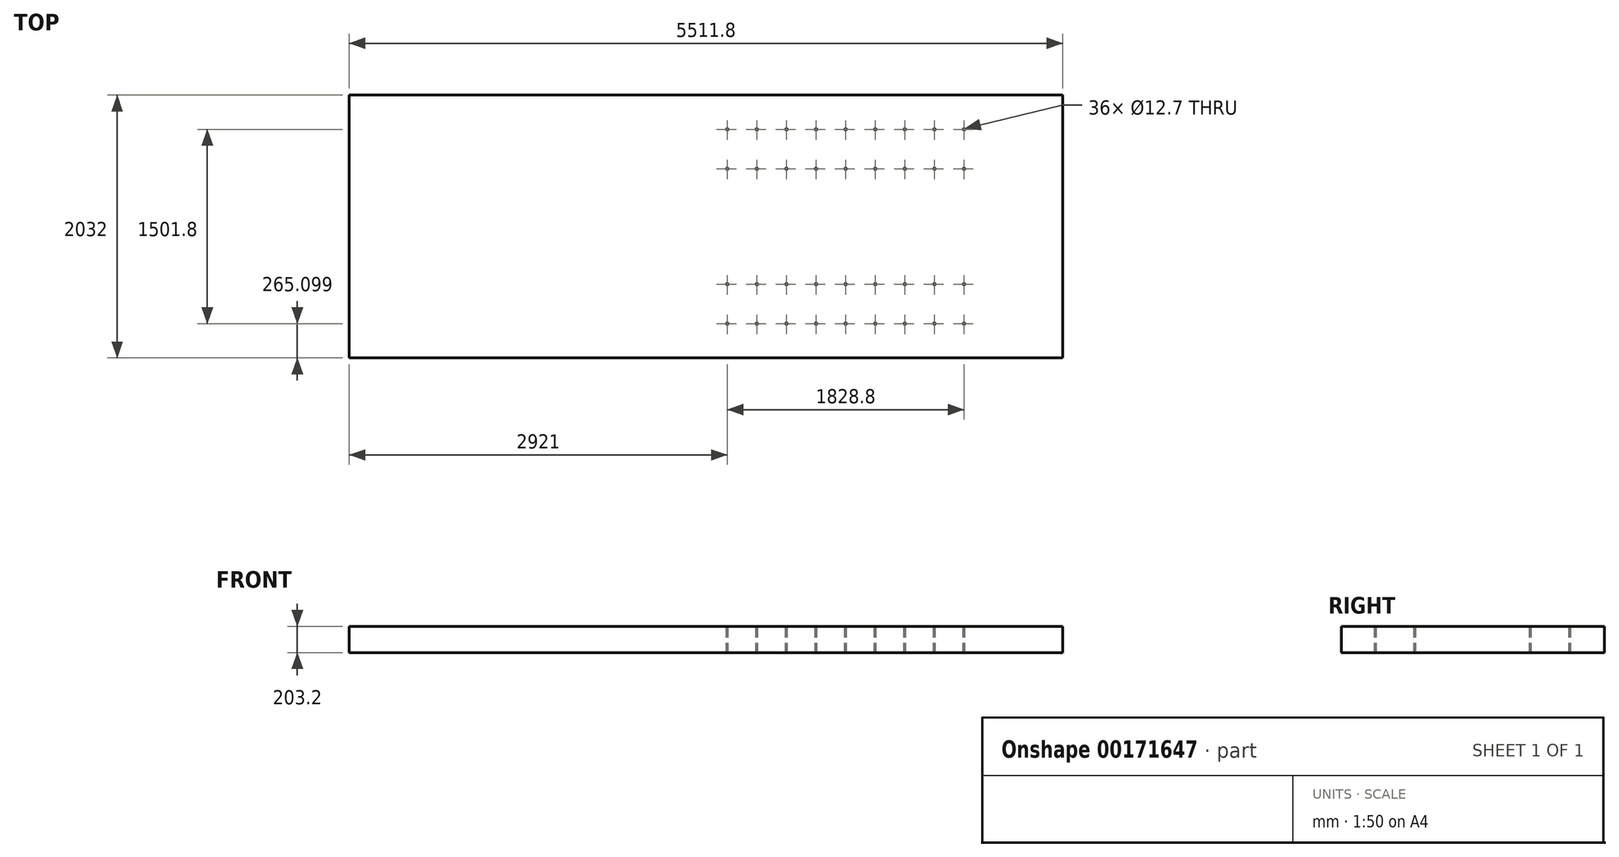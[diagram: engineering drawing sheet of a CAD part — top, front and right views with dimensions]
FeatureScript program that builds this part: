
annotation { "Feature Type Name" : "Feature", "Feature Type Description" : "" }
export const myFeature = defineFeature(function(context is Context, id is Id, definition is map)
    precondition{}
    {
        {
            var Q0;
            Q0=qCreatedBy(makeId("Top.planeOp"),FACE);
            var sketch = newSketch(context, id + "F0", { "sketchPlane" : qUnion([Q0])});
            skLineSegment(sketch, "E0.bottom", {"start": v(2755.9, 1016) * mm, "end": v(-2755.9, 1016) * mm});
            skLineSegment(sketch, "E0.top", {"start": v(2755.9, -1016) * mm, "end": v(-2755.9, -1016) * mm});
            skLineSegment(sketch, "E0.left", {"start": v(2755.9, 1016) * mm, "end": v(2755.9, -1016) * mm});
            skLineSegment(sketch, "E0.right", {"start": v(-2755.9, 1016) * mm, "end": v(-2755.9, -1016) * mm});
            skSolve(sketch);
        }
        {
            var Q0;
            Q0=makeQuery(id+"F0.imprint","IMPRINT",FACE,{"disambiguationData":[TD([[makeQuery(id+"F0.imprint","IMPRINT",EDGE,{"derivedFrom":sQuery(id+"F0.wireOp",EDGE,"E0.bottom")}),1.0]])]});
            extrude(context, id + "F1", {"entities" : qUnion([Q0]), "depth" : 203.2 * mm});
        }
        {
            var Q0;
            Q0=makeQuery(id+"F1.opExtrude","CAP_FACE",FACE,{"disambiguationData":[OSD([sQuery(id+"F0.wireOp",EDGE,"E0.bottom"),sQuery(id+"F0.wireOp",EDGE,"E0.top"),sQuery(id+"F0.wireOp",EDGE,"E0.left"),sQuery(id+"F0.wireOp",EDGE,"E0.right")])],"isStart":true});
            var sketch = newSketch(context, id + "F2", { "sketchPlane" : qUnion([Q0])});
            skPoint(sketch, "E1", {"position": v(1993.9, 750.9) * mm});
            skPoint(sketch, "E2", {"position": v(1765.3, 750.9) * mm});
            skPoint(sketch, "E3", {"position": v(1536.7, 750.9) * mm});
            skPoint(sketch, "E4", {"position": v(1079.5, 750.9) * mm});
            skPoint(sketch, "E5", {"position": v(393.7, 750.9) * mm});
            skPoint(sketch, "E6", {"position": v(622.3, 750.9) * mm});
            skPoint(sketch, "E7", {"position": v(850.9, 750.9) * mm});
            skPoint(sketch, "E8", {"position": v(1308.1, 750.9) * mm});
            skPoint(sketch, "E9", {"position": v(165.1, 750.9) * mm});
            skPoint(sketch, "E10.MirrorP", {"position": v(1993.9, 446.1) * mm});
            skPoint(sketch, "E11.MirrorP", {"position": v(1765.3, 446.1) * mm});
            skPoint(sketch, "E12.MirrorP", {"position": v(1536.7, 446.1) * mm});
            skPoint(sketch, "E13.MirrorP", {"position": v(1308.1, 446.1) * mm});
            skPoint(sketch, "E14.MirrorP", {"position": v(1079.5, 446.1) * mm});
            skPoint(sketch, "E15.MirrorP", {"position": v(850.9, 446.1) * mm});
            skPoint(sketch, "E16.MirrorP", {"position": v(622.3, 446.1) * mm});
            skPoint(sketch, "E17.MirrorP", {"position": v(393.7, 446.1) * mm});
            skPoint(sketch, "E18.MirrorP", {"position": v(165.1, 446.1) * mm});
            skPoint(sketch, "E19.MirrorP", {"position": v(1993.9, -446.1) * mm});
            skPoint(sketch, "E20.MirrorP", {"position": v(1308.1, -750.9) * mm});
            skPoint(sketch, "E21.MirrorP", {"position": v(1765.3, -446.1) * mm});
            skPoint(sketch, "E22.MirrorP", {"position": v(850.9, -446.1) * mm});
            skPoint(sketch, "E23.MirrorP", {"position": v(622.3, -446.1) * mm});
            skPoint(sketch, "E24.MirrorP", {"position": v(1079.5, -446.1) * mm});
            skPoint(sketch, "E25.MirrorP", {"position": v(1079.5, -750.9) * mm});
            skPoint(sketch, "E26.MirrorP", {"position": v(850.9, -750.9) * mm});
            skPoint(sketch, "E27.MirrorP", {"position": v(393.7, -750.9) * mm});
            skPoint(sketch, "E28.MirrorP", {"position": v(1993.9, -750.9) * mm});
            skPoint(sketch, "E29.MirrorP", {"position": v(165.1, -446.1) * mm});
            skPoint(sketch, "E30.MirrorP", {"position": v(1308.1, -446.1) * mm});
            skPoint(sketch, "E31.MirrorP", {"position": v(165.1, -750.9) * mm});
            skPoint(sketch, "E32.MirrorP", {"position": v(1765.3, -750.9) * mm});
            skPoint(sketch, "E33.MirrorP", {"position": v(1536.7, -750.9) * mm});
            skPoint(sketch, "E34.MirrorP", {"position": v(1536.7, -446.1) * mm});
            skPoint(sketch, "E35.MirrorP", {"position": v(622.3, -750.9) * mm});
            skPoint(sketch, "E36.MirrorP", {"position": v(393.7, -446.1) * mm});
            skSolve(sketch);
        }
        {
            var Q0;
            Q0=sQuery(id+"F2.wireOp",VERTEX,"E5");
            var Q1;
            Q1=sQuery(id+"F2.wireOp",VERTEX,"E4");
            var Q2;
            Q2=sQuery(id+"F2.wireOp",VERTEX,"E3");
            var Q3;
            Q3=sQuery(id+"F2.wireOp",VERTEX,"E2");
            var Q4;
            Q4=sQuery(id+"F2.wireOp",VERTEX,"E1");
            var Q5;
            Q5=sQuery(id+"F2.wireOp",VERTEX,"E32.MirrorP");
            var Q6;
            Q6=sQuery(id+"F2.wireOp",VERTEX,"E15.MirrorP");
            var Q7;
            Q7=sQuery(id+"F2.wireOp",VERTEX,"E33.MirrorP");
            var Q8;
            Q8=sQuery(id+"F2.wireOp",VERTEX,"E14.MirrorP");
            var Q9;
            Q9=sQuery(id+"F2.wireOp",VERTEX,"E13.MirrorP");
            var Q10;
            Q10=sQuery(id+"F2.wireOp",VERTEX,"E35.MirrorP");
            var Q11;
            Q11=sQuery(id+"F2.wireOp",VERTEX,"E12.MirrorP");
            var Q12;
            Q12=sQuery(id+"F2.wireOp",VERTEX,"E36.MirrorP");
            var Q13;
            Q13=sQuery(id+"F2.wireOp",VERTEX,"E19.MirrorP");
            var Q14;
            Q14=sQuery(id+"F2.wireOp",VERTEX,"E30.MirrorP");
            var Q15;
            Q15=sQuery(id+"F2.wireOp",VERTEX,"E25.MirrorP");
            var Q16;
            Q16=sQuery(id+"F2.wireOp",VERTEX,"E27.MirrorP");
            var Q17;
            Q17=sQuery(id+"F2.wireOp",VERTEX,"E11.MirrorP");
            var Q18;
            Q18=sQuery(id+"F2.wireOp",VERTEX,"E16.MirrorP");
            var Q19;
            Q19=sQuery(id+"F2.wireOp",VERTEX,"E34.MirrorP");
            var Q20;
            Q20=sQuery(id+"F2.wireOp",VERTEX,"E17.MirrorP");
            var Q21;
            Q21=sQuery(id+"F2.wireOp",VERTEX,"E28.MirrorP");
            var Q22;
            Q22=sQuery(id+"F2.wireOp",VERTEX,"E18.MirrorP");
            var Q23;
            Q23=sQuery(id+"F2.wireOp",VERTEX,"E29.MirrorP");
            var Q24;
            Q24=sQuery(id+"F2.wireOp",VERTEX,"E20.MirrorP");
            var Q25;
            Q25=sQuery(id+"F2.wireOp",VERTEX,"E22.MirrorP");
            var Q26;
            Q26=sQuery(id+"F2.wireOp",VERTEX,"E21.MirrorP");
            var Q27;
            Q27=sQuery(id+"F2.wireOp",VERTEX,"E24.MirrorP");
            var Q28;
            Q28=sQuery(id+"F2.wireOp",VERTEX,"E23.MirrorP");
            var Q29;
            Q29=sQuery(id+"F2.wireOp",VERTEX,"E26.MirrorP");
            var Q30;
            Q30=sQuery(id+"F2.wireOp",VERTEX,"E31.MirrorP");
            var Q31;
            Q31=sQuery(id+"F2.wireOp",VERTEX,"E10.MirrorP");
            var Q32;
            Q32=sQuery(id+"F2.wireOp",VERTEX,"E9");
            var Q33;
            Q33=sQuery(id+"F2.wireOp",VERTEX,"E8");
            var Q34;
            Q34=sQuery(id+"F2.wireOp",VERTEX,"E7");
            var Q35;
            Q35=sQuery(id+"F2.wireOp",VERTEX,"E6");
            var Q36;
            Q36=makeQuery(id+"F1.opExtrude","SWEPT_BODY",BODY,{"disambiguationData":[OSD([sQuery(id+"F0.wireOp",EDGE,"E0.bottom"),sQuery(id+"F0.wireOp",EDGE,"E0.top"),sQuery(id+"F0.wireOp",EDGE,"E0.left"),sQuery(id+"F0.wireOp",EDGE,"E0.right")])]});
            hole(context, id + "F3", {"style" : HoleStyle.SIMPLE, "endStyle" : HoleEndStyle.THROUGH, "holeDiameter" : 12.7 * mm, "locations" : qUnion([Q0, Q1, Q2, Q3, Q4, Q5, Q6, Q7, Q8, Q9, Q10, Q11, Q12, Q13, Q14, Q15, Q16, Q17, Q18, Q19, Q20, Q21, Q22, Q23, Q24, Q25, Q26, Q27, Q28, Q29, Q30, Q31, Q32, Q33, Q34, Q35]), "scope" : qUnion([Q36]), "isTappedThrough" : true});
        }
    });
